# Revit family: IS_iLifeS_T4740_BIM_NL
name_source: partatom
category: Plumbing Fixtures
units: mm (PartAtom-declared; Revit-internal decimal feet)

## family parameters
Always vertical = No
Cut with Voids When Loaded = No
OmniClass Number = 23.45.05.14.14
OmniClass Title = Sinks/Lavatories
Part Type = Normal
Room Calculation Point = No
Round Connector Dimension = Use Diameter
Shared = No
Work Plane-Based = No

## types (2) — shared parameters
Accessories = https://www.idealstandard.nl
Afmetingen = 340 x 263 x 176 mm
AfstandsEenheid = Millimeter
AreaUnits = millimetres
AssetType = Fixed
Auteur = Ideal Standard
BIMObjectName = IS_IdealStandard_Pedestal washbasins_i.lifeS_T4740
BIMobject category = Wash Basins
BIMobject category code = wash-basins
BIMobject main category = Sanitary
BIMobject main category code = sanitary
Beschrijvinggarantie = Herstellergarantie
BimObjectNaam = IS_IdealStandard_Pedestal washbasins_i.lifeS_T4740
Brand = Ideal Standard
Brand url = https://www.idealstandard.nl
Breedte = 175.469376
Category = Sanitary
ConnectionType = Plumbing
CurrencyUnit = €
CurrentRevision = 1
Date of publishing = 27/05/2022
Diepte = 263 mm
DurationUnit = Years
DuurEenheid = Jahre
Edition number = 1
ElementType = Fixed
ExpectedLife = 99
Garantieunits = Jahre
Help = https://www.idealstandard.nl
Hoogte = 340.000088367409
Hulp = https://www.idealstandard.nl
IFC Classification = Sanitary Terminal
Installatieinstructies = https://www.idealstandard.nl
Installation instructions = https://www.idealstandard.nl
InstallationInstructions = https://www.idealstandard.nl
IsAutomaticFlush = No
Lengte = 263 mm
LinearUnits = Millimetres
MaintenanceInformation = https://www.idealstandard.nl
Manufacturer = Ideal Standard
Manufacturer name = Ideal Standard
ManufacturerURL = https://www.idealstandard.nl
Materiaal = Feiner Schamotte
Material = Finefireclay
Material main = Finefireclay
Merk = Ideal Standard
ModelReference = i.life S semipedestal
NBS Reference Code = 45-35-70/365
NBS Reference Description = Pedestal wash basins
Name = Pedestal washbasins_i.lifeS_T4740_IdealStandard
NettWeight = 6.1
Nettogewicht = 6.1
NominalDepth = 263 mm
NominalHeight = 340 mm
NominalLength = 263 mm
NominalWidth = 175 mm
Normen = Pedestal washbasins_i.lifeS_T4740_IdealStandard
OmniClass Code = 23-21 25 23 15
OmniClass Description = Pedestals
OppervlakteEenheid = Millimeter
PredefinedType = Sanitary
Product Guid = 0ba25821-fc50-4b4a-97ae-1c8177d799f6
Product SKU = T4740
Product certification = https://www.idealstandard.nl
Product data url = https://bimobject.com
Product family = I.life S
Product group = Sanitary: Pedestals
Product name = i.life S semipedestal
Product url = https://www.idealstandard.nl
ProductInformation = https://www.idealstandard.nl
Productinformatie = https://www.idealstandard.nl
QR code = http://bimobject.com
Referentie = i.life S semipedestal
ReplacementCost = 0
Revisie = 1
Shape = Sculpture
Size = 340 x 263 x 176 mm
Space = Internal
SpareParts = https://www.idealstandard.nl
Technical description = https://www.idealstandard.nl
Telefoonnummer = 077 355 08 08
Typeconnectie = Installation
UNSPSC Code = 301815
URL = https://www.idealstandard.nl
Uniclass 2015 Code = Pr_40_20_96_63
Uniclass 2015 Name = Pedestal washbasins
Uniclass2015Beschrijving = Pedestal washbasins
Uniclass2015Code = Pr_40_20_96_63
Uniclass2015Referentie = Pr_40_20_96_63
Uniclass2015Title = Pedestal washbasins
Uniclass2015Version = v.25
Urlproducent = https://www.idealstandard.nl
ValutaEenheid = Euro
Versie = 1
Version = 1
VolumeUnits = Litres
Volumeunits = Liter
Vorm = geformt
WRASURL = https://www.wrasapprovals.co.uk
WarrantyDescription = manufacturer warranty
WarrantyDurationUnit = years
Wisselstukken = https://www.idealstandard.nl
Youtube clip = https://www.youtube.com
zero-valued in all types: BrutoGewicht, Cost, Vervangingskosten

## per-type parameters (varying)
| type | Afwerking | Artikelnummer | Artikelomschrijving | BarCode | Color | Description | Eigenschappen | Features | Finish | GTIN code | Kleur | MainColor | Model | ModelNumber |
| T474001 - i.life S semipedestal - White | Weiß | T474001 | Ideal Standard i.life S Halbsäule, inkl. L-Wandhalterung, für Becken i.life S & i.life B 45 cm, weiß, im Karton, EU-Palette | 8014140491866 | Weiß | Ideal Standard i.life S semipedestal, incl. L-shape wall-fixation, for basins i.life S & i.life B 45 cm, white, in carton box, EU pallet | Halbsockel, inkl. L-Wandhalterung, für Becken i.life S & i.life B 45 cm, weiß, im Karton, EU-Palette | semipedestal, incl. L-shape wall-fixation, for basins i.life S & i.life B 45 cm, white, in carton box, EU pallet | White | https://8014140491866 | Weiß | White | T474001 | T474001 |
| T4740MA - i.life S semipedestal - Ideal Plus White | Ideales Plus-Weiß | T4740MA | Ideal Standard i.life S Halbsäule, inkl. L-Wandhalterung, für Becken i.life S & i.life B 45 cm, weiß Ideal Plus, im Karton, EU-Palette | 8014140491873 | Ideales Plus-Weiß | Ideal Standard i.life S semipedestal, incl. L-shape wall-fixation, for basins i.life S & i.life B 45 cm, white Ideal Plus, in carton box, EU pallet | Halbsockel, inkl. L-Wandhalterung, für Becken i.life S & i.life B 45 cm, weiß Ideal Plus, im Karton, EU-Palette | semipedestal, incl. L-shape wall-fixation, for basins i.life S & i.life B 45 cm, white Ideal Plus, in carton box, EU pallet | Ideal Plus White | https://8014140491873 | Ideales Plus-Weiß | Ideal Plus White | T4740MA | T4740MA |

## geometry (parser evidence)
native form markers: Sweep x3
no freeform markers — native parametric forms only
